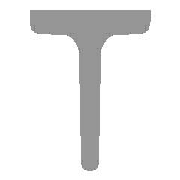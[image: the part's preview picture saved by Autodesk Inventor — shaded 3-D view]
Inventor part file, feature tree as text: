
AUTODESK INVENTOR PART (.ipt)
format: ipt  version: 2020.1 (Build 241239000, 239)  size: 154,624 bytes
history: native  units: mm (DEFAULTED — no unit token found)
features: other x4, sketch x3, plane x2
ambient origin geometry x7: Origin, YZ Plane, XY Plane, X Axis, Y Axis, Z Axis, Center Point
bodies: Solid1 (feature_tree), Body (feature_tree)
feature tree (9):
  parser-record x1  (decoder bookkeeping rows leaked as tree rows — omitted from the tree; the rows remain in map.json)
  other  "Driven Length"
  other  "Start plane"
  other  "End plane"
  plane  "WorkPlane3"
  sketch  "Sketch"  dims[d5=0.0mm d7=0.00349mm d8=2.75mm d9=3.85mm d10=2.75mm d11=3.85mm d12=0.00349mm d13=900.0mm d14=0.0mm d23=3.7mm d26=0.199973mm d27=0.199973mm d28=4.0mm d29=2.0mm d30=1.0mm d31=30.0mm d32=0.199973mm d33=30.0mm d34=8.5mm d35=-0.0mm d36=900.0mm d37=90.0deg d38=900.0mm]
  sketch  "Sketch3"  dims[d2=50.0mm]
  plane  "Work Plane6"
  sketch  "Sketch4"  dims[d4=0.00698mm]
